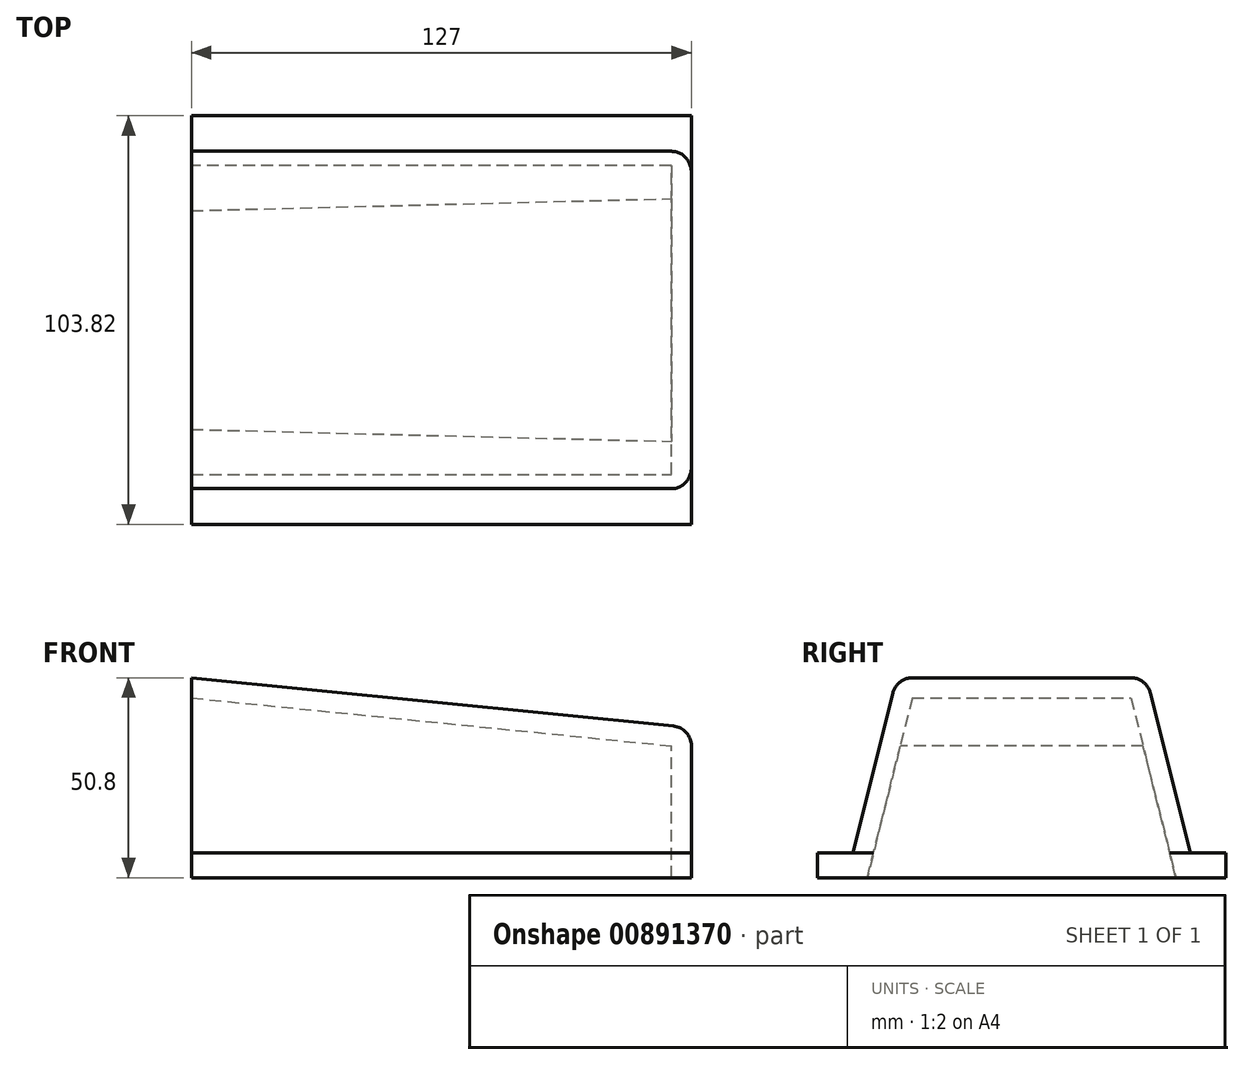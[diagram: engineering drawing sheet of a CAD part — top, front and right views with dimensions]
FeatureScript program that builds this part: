
annotation { "Feature Type Name" : "Feature", "Feature Type Description" : "" }
export const myFeature = defineFeature(function(context is Context, id is Id, definition is map)
    precondition{}
    {
        {
            var Q0;
            Q0=qCreatedBy(makeId("Top.planeOp"),FACE);
            var sketch = newSketch(context, id + "F0", { "sketchPlane" : qUnion([Q0])});
            skLineSegment(sketch, "E0.bottom", {"start": v(63.5, -44.45) * mm, "end": v(-63.5, -44.45) * mm});
            skLineSegment(sketch, "E0.top", {"start": v(63.5, 44.45) * mm, "end": v(-63.5, 44.45) * mm});
            skLineSegment(sketch, "E0.left", {"start": v(63.5, -44.45) * mm, "end": v(63.5, 44.45) * mm});
            skLineSegment(sketch, "E0.right", {"start": v(-63.5, -44.45) * mm, "end": v(-63.5, 44.45) * mm});
            skPoint(sketch, "E0.middle", {"position": v(0, 0) * mm});
            skSolve(sketch);
        }
        {
            var Q0;
            Q0=makeQuery(id+"F0.imprint","IMPRINT",FACE,{"disambiguationData":[TD([[makeQuery(id+"F0.imprint","IMPRINT",EDGE,{"derivedFrom":sQuery(id+"F0.wireOp",EDGE,"E0.bottom")}),-1.0]])]});
            extrude(context, id + "F1", {"entities" : qUnion([Q0]), "depth" : 50.8 * mm, "offsetDistance" : 25.4 * mm});
        }
        {
            var Q0;
            Q0=makeQuery(id+"F1.opExtrude","CAP_EDGE",EDGE,{"disambiguationData":[OSD([sQuery(id+"F0.wireOp",EDGE,"E0.top")])],"isStart":false});
            var Q1;
            Q1=makeQuery(id+"F1.opExtrude","CAP_EDGE",EDGE,{"disambiguationData":[OSD([sQuery(id+"F0.wireOp",EDGE,"E0.bottom")])],"isStart":false});
            chamfer(context, id + "F2", {"entities" : qUnion([Q0, Q1]), "chamferType" : ChamferType.TWO_OFFSETS, "width1" : 12.7 * mm, "oppositeDirection" : false, "width2" : 50.8 * mm, "tangentPropagation" : true});
        }
        {
            var Q0;
            Q0=makeQuery(id+"F1.opExtrude","CAP_EDGE",EDGE,{"disambiguationData":[OSD([sQuery(id+"F0.wireOp",EDGE,"E0.left")])],"isStart":false});
            chamfer(context, id + "F3", {"entities" : qUnion([Q0]), "chamferType" : ChamferType.TWO_OFFSETS, "width1" : 127 * mm, "oppositeDirection" : false, "width2" : 12.7 * mm, "tangentPropagation" : true});
        }
        {
            var Q0;
            Q0=makeQuery(id+"F1.opExtrude","CAP_FACE",FACE,{"disambiguationData":[OSD([sQuery(id+"F0.wireOp",EDGE,"E0.bottom"),sQuery(id+"F0.wireOp",EDGE,"E0.top"),sQuery(id+"F0.wireOp",EDGE,"E0.left"),sQuery(id+"F0.wireOp",EDGE,"E0.right")])],"isStart":true});
            var Q1;
            Q1=makeQuery(id+"F1.opExtrude","SWEPT_FACE",FACE,{"disambiguationData":[OSD([sQuery(id+"F0.wireOp",EDGE,"E0.right")])]});
            shell(context, id + "F4", {"entities" : qUnion([Q0, Q1]), "thickness" : 5.08 * mm});
        }
        {
            var Q0;
            Q0=makeQuery(id+"F1.opExtrude","CAP_FACE",FACE,{"disambiguationData":[OSD([sQuery(id+"F0.wireOp",EDGE,"E0.bottom"),sQuery(id+"F0.wireOp",EDGE,"E0.top"),sQuery(id+"F0.wireOp",EDGE,"E0.left"),sQuery(id+"F0.wireOp",EDGE,"E0.right")])],"isStart":true});
            var sketch = newSketch(context, id + "F5", { "sketchPlane" : qUnion([Q0])});
            skLineSegment(sketch, "E1.bottom", {"start": v(-63.5, 39.21) * mm, "end": v(63.5, 39.21) * mm});
            skLineSegment(sketch, "E1.top", {"start": v(-63.5, 51.91) * mm, "end": v(63.5, 51.91) * mm});
            skLineSegment(sketch, "E1.left", {"start": v(-63.5, 39.21) * mm, "end": v(-63.5, 51.91) * mm});
            skLineSegment(sketch, "E1.right", {"start": v(63.5, 39.21) * mm, "end": v(63.5, 51.91) * mm});
            skLineSegment(sketch, "E2.bottom", {"start": v(-63.5, -39.21) * mm, "end": v(63.5, -39.21) * mm});
            skLineSegment(sketch, "E2.top", {"start": v(-63.5, -51.91) * mm, "end": v(63.5, -51.91) * mm});
            skLineSegment(sketch, "E2.left", {"start": v(-63.5, -39.21) * mm, "end": v(-63.5, -51.91) * mm});
            skLineSegment(sketch, "E2.right", {"start": v(63.5, -39.21) * mm, "end": v(63.5, -51.91) * mm});
            skSolve(sketch);
        }
        {
            var Q0;
            {var subQ0=sQuery(id+"F5.wireOp",EDGE,"E1.top");Q0=makeQuery(id+"F5.imprint","IMPRINT",FACE,{"disambiguationData":[TD([[makeQuery(id+"F5.imprint","IMPRINT",EDGE,{"derivedFrom":subQ0}),-1.0]])]});}
            var Q1;
            {var subQ0=sQuery(id+"F5.wireOp",EDGE,"E1.left");var subQ4=sQuery(id+"F5.wireOp",EDGE,"E1.bottom");var subQ5=makeQuery(id+"F5.imprint","INTERSECT",VERTEX,{"derivedFrom":[subQ4,subQ0]});Q1=makeQuery(id+"F5.imprint","IMPRINT",FACE,{"disambiguationData":[TD([[makeQuery(id+"F5.imprint","IMPRINT",EDGE,{"disambiguationData":[TD([[subQ5,1.0]])],"derivedFrom":subQ4}),-1.0]])]});}
            var Q2;
            {var subQ0=sQuery(id+"F5.wireOp",EDGE,"E2.top");Q2=makeQuery(id+"F5.imprint","IMPRINT",FACE,{"disambiguationData":[TD([[makeQuery(id+"F5.imprint","IMPRINT",EDGE,{"derivedFrom":subQ0}),1.0]])]});}
            var Q3;
            {var subQ0=sQuery(id+"F5.wireOp",EDGE,"E2.left");var subQ4=sQuery(id+"F5.wireOp",EDGE,"E2.bottom");var subQ5=makeQuery(id+"F5.imprint","INTERSECT",VERTEX,{"derivedFrom":[subQ4,subQ0]});Q3=makeQuery(id+"F5.imprint","IMPRINT",FACE,{"disambiguationData":[TD([[makeQuery(id+"F5.imprint","IMPRINT",EDGE,{"disambiguationData":[TD([[subQ5,1.0]])],"derivedFrom":subQ4}),1.0]])]});}
            extrude(context, id + "F6", {"entities" : qUnion([Q0, Q1, Q2, Q3]), "operationType" : NewBodyOperationType.ADD, "oppositeDirection" : true, "depth" : 6.35 * mm, "offsetDistance" : 25.4 * mm});
        }
        {
            var Q0;
            Q0=makeQuery(id+"F3.opChamfer","BLEND_EDGE",EDGE,{"blendedFrom":[makeQuery(id+"F1.opExtrude","CAP_EDGE",EDGE,{"disambiguationData":[OSD([sQuery(id+"F0.wireOp",EDGE,"E0.left")])],"isStart":false}),makeQuery(id+"F2.opChamfer","BLEND_FACE",FACE,{"disambiguationData":[OSD([sQuery(id+"F0.wireOp",EDGE,"E0.top")])]})],"blendedInto":[makeQuery(id+"F2.opChamfer","BLEND_FACE",FACE,{"disambiguationData":[OSD([sQuery(id+"F0.wireOp",EDGE,"E0.top")])]})]});
            var Q1;
            Q1=makeQuery(id+"F3.opChamfer","BLEND_EDGE",EDGE,{"blendedFrom":[makeQuery(id+"F1.opExtrude","CAP_EDGE",EDGE,{"disambiguationData":[OSD([sQuery(id+"F0.wireOp",EDGE,"E0.left")])],"isStart":false}),makeQuery(id+"F2.opChamfer","BLEND_FACE",FACE,{"disambiguationData":[OSD([sQuery(id+"F0.wireOp",EDGE,"E0.bottom")])]})],"blendedInto":[makeQuery(id+"F2.opChamfer","BLEND_FACE",FACE,{"disambiguationData":[OSD([sQuery(id+"F0.wireOp",EDGE,"E0.bottom")])]})]});
            var Q2;
            {var subQ0=sQuery(id+"F0.wireOp",EDGE,"E0.left");Q2=makeQuery(id+"F3.opChamfer","BLEND_EDGE",EDGE,{"blendedFrom":[makeQuery(id+"F1.opExtrude","CAP_EDGE",EDGE,{"disambiguationData":[OSD([subQ0])],"isStart":false}),makeQuery(id+"F1.opExtrude","SWEPT_FACE",FACE,{"disambiguationData":[OSD([subQ0])]})],"blendedInto":[makeQuery(id+"F1.opExtrude","SWEPT_FACE",FACE,{"disambiguationData":[OSD([subQ0])]})]});}
            var Q3;
            Q3=makeQuery(id+"F2.opChamfer","BLEND_EDGE",EDGE,{"blendedFrom":[makeQuery(id+"F1.opExtrude","CAP_EDGE",EDGE,{"disambiguationData":[OSD([sQuery(id+"F0.wireOp",EDGE,"E0.top")])],"isStart":false}),makeQuery(id+"F1.opExtrude","SWEPT_FACE",FACE,{"disambiguationData":[OSD([sQuery(id+"F0.wireOp",EDGE,"E0.left")])]})],"blendedInto":[makeQuery(id+"F1.opExtrude","SWEPT_FACE",FACE,{"disambiguationData":[OSD([sQuery(id+"F0.wireOp",EDGE,"E0.left")])]})]});
            var Q4;
            Q4=makeQuery(id+"F2.opChamfer","BLEND_EDGE",EDGE,{"blendedFrom":[makeQuery(id+"F1.opExtrude","CAP_EDGE",EDGE,{"disambiguationData":[OSD([sQuery(id+"F0.wireOp",EDGE,"E0.bottom")])],"isStart":false}),makeQuery(id+"F1.opExtrude","SWEPT_FACE",FACE,{"disambiguationData":[OSD([sQuery(id+"F0.wireOp",EDGE,"E0.left")])]})],"blendedInto":[makeQuery(id+"F1.opExtrude","SWEPT_FACE",FACE,{"disambiguationData":[OSD([sQuery(id+"F0.wireOp",EDGE,"E0.left")])]})]});
            fillet(context, id + "F7", {"entities" : qUnion([Q0, Q1, Q2, Q3, Q4]), "radius" : 5.08 * mm, "tangentPropagation" : true, "allowEdgeOverflow" : false});
        }
    });
